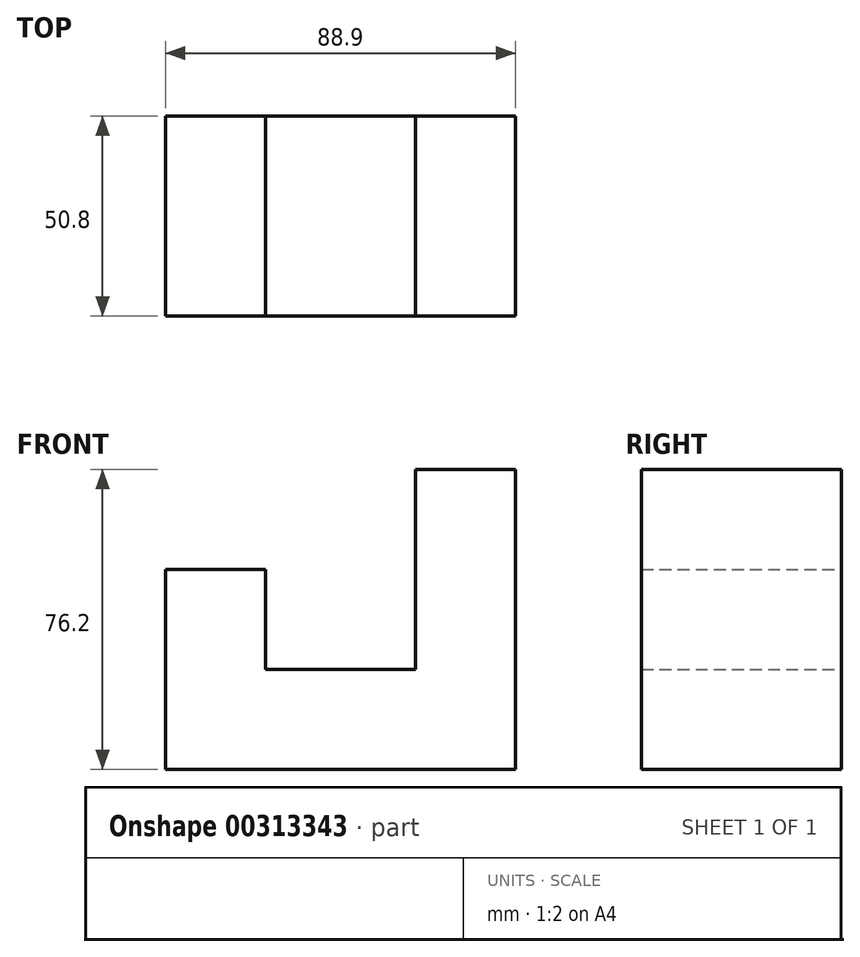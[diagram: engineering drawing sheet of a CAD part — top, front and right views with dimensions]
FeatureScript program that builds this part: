
annotation { "Feature Type Name" : "Feature", "Feature Type Description" : "" }
export const myFeature = defineFeature(function(context is Context, id is Id, definition is map)
    precondition{}
    {
        {
            var Q0;
            Q0=qCreatedBy(makeId("Front.planeOp"),FACE);
            var sketch = newSketch(context, id + "F0", { "sketchPlane" : qUnion([Q0])});
            skLineSegment(sketch, "E0", {"start": v(-45.51, -47.94) * mm, "end": v(43.39, -47.94) * mm});
            skLineSegment(sketch, "E1", {"start": v(-45.51, -47.94) * mm, "end": v(-45.51, 2.86) * mm});
            skLineSegment(sketch, "E2", {"start": v(-45.51, 2.86) * mm, "end": v(-20.11, 2.86) * mm});
            skLineSegment(sketch, "E3", {"start": v(-20.11, 2.86) * mm, "end": v(-20.11, -22.54) * mm});
            skLineSegment(sketch, "E4", {"start": v(-20.11, -22.54) * mm, "end": v(17.99, -22.54) * mm});
            skLineSegment(sketch, "E5", {"start": v(17.99, -22.54) * mm, "end": v(17.99, 28.26) * mm});
            skLineSegment(sketch, "E6", {"start": v(17.99, 28.26) * mm, "end": v(43.39, 28.26) * mm});
            skLineSegment(sketch, "E7", {"start": v(43.39, 28.26) * mm, "end": v(43.39, -47.94) * mm});
            skSolve(sketch);
        }
        {
            var Q0;
            Q0=makeQuery(id+"F0.imprint","IMPRINT",FACE,{"disambiguationData":[TD([[makeQuery(id+"F0.imprint","IMPRINT",EDGE,{"derivedFrom":sQuery(id+"F0.wireOp",EDGE,"E0")}),1.0]])]});
            extrude(context, id + "F1", {"entities" : qUnion([Q0]), "depth" : 50.8 * mm});
        }
    });
